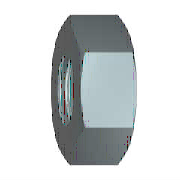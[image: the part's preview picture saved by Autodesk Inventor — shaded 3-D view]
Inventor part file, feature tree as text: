
AUTODESK INVENTOR PART (.ipt)
format: ipt  version: 2013 (Build 170138000, 138)  size: 171,520 bytes
history: native  units: mm (DEFAULTED — no unit token found)
features: sketch x3, chamfer x1, hole x1, other x1, plane x1
ambient origin geometry x7: Origin, YZ Plane, XZ Plane, X Axis, Y Axis, Z Axis, Center Point
bodies: Solid1 (feature_tree), Body (feature_tree)
feature tree (7):
  chamfer  "Chamfer1"  Angle=30.0deg  [1 undecoded]
  hole  "Thread"  [1 undecoded]
  other  "Work Axis1"
  plane  "Work Plane1"
  sketch  "Sketch1"  dims[d0=21.997045mm]
  sketch  "Sketch2"  dims[d1=11.1252mm]
  sketch  "Sketch3"  dims[d2=0.0mm d3=30.0deg d4=30.0deg d5=19.05mm d6=19.05mm d7=90.0deg d25=10.5918mm d26=6.0mm d27=4.0mm d28=2.0mm d29=14.3117mm d30=8.0mm d31=20.594885mm d8=1.05755mm d9=30.0deg d10=1.05755mm d11=30.0deg d13=0.0mm d14=0.0mm d39=0.0mm d40=1.05755mm d41=1.05755mm d42=0.0mm]
note: 2 required parameter values undecoded (feature->parameter linkage not recoverable at this tier; creation-order binding heuristic only, values carry confidence <= 0.55)
